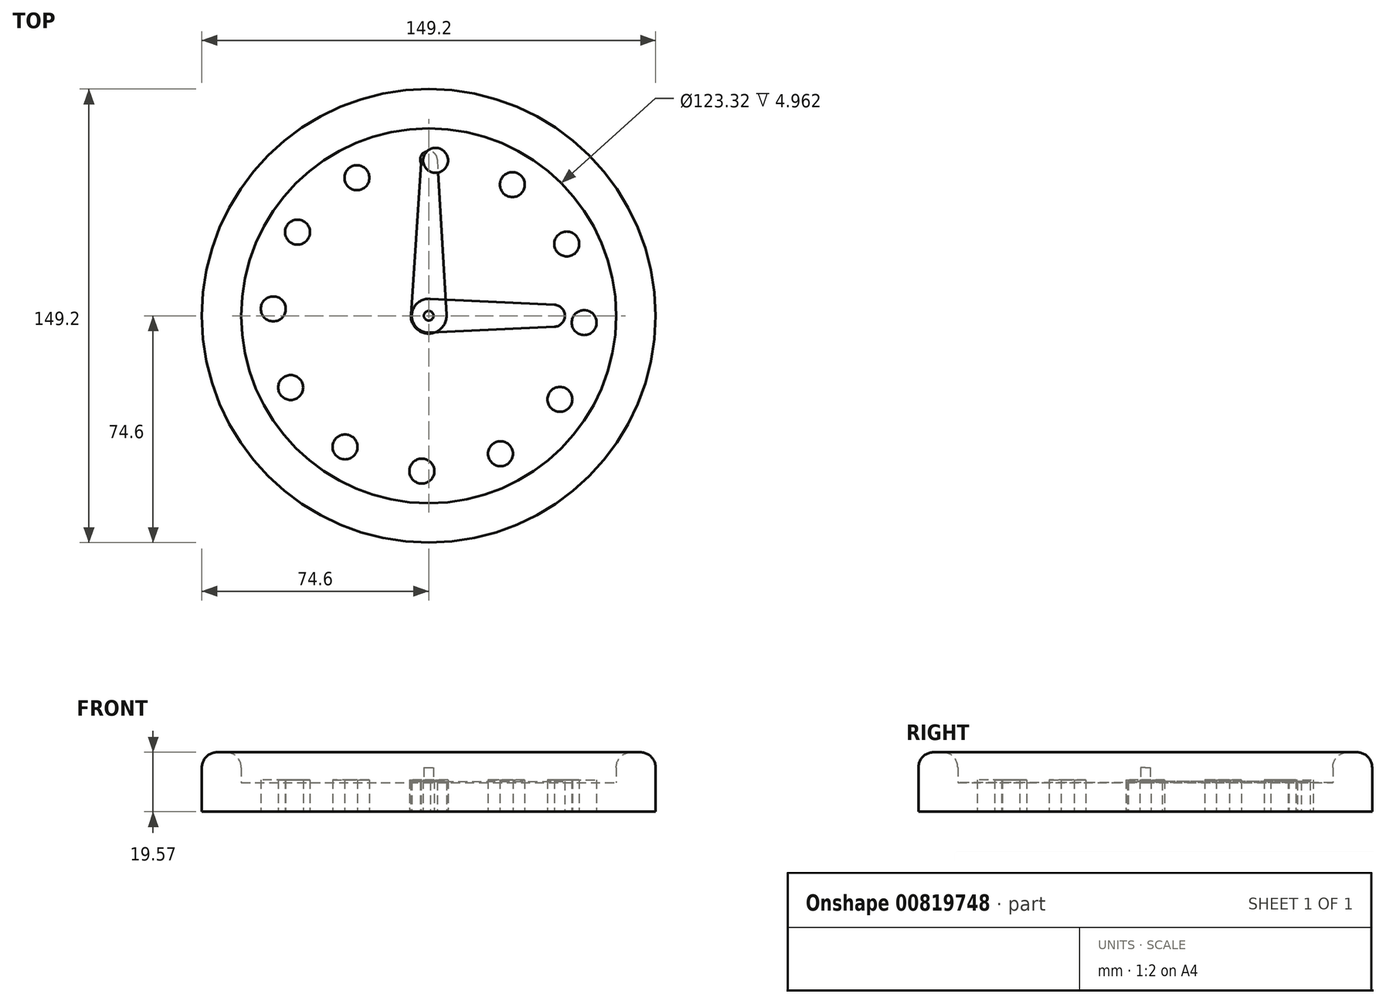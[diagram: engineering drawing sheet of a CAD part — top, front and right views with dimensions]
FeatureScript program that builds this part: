
annotation { "Feature Type Name" : "Feature", "Feature Type Description" : "" }
export const myFeature = defineFeature(function(context is Context, id is Id, definition is map)
    precondition{}
    {
        {
            var Q0;
            Q0=qCreatedBy(makeId("Front.planeOp"),FACE);
            var sketch = newSketch(context, id + "F0", { "sketchPlane" : qUnion([Q0])});
            skLineSegment(sketch, "E0", {"start": v(0, 0) * mm, "end": v(0, 64.16) * mm, "construction": true});
            skLineSegment(sketch, "E1.bottom", {"start": v(0, 0) * mm, "end": v(-74.6, 0) * mm});
            skLineSegment(sketch, "E1.top", {"start": v(0, 9.6) * mm, "end": v(-61.66, 9.6) * mm});
            skLineSegment(sketch, "E1.left", {"start": v(0, 0) * mm, "end": v(0, 9.6) * mm});
            skLineSegment(sketch, "E1.right", {"start": v(-74.6, 0) * mm, "end": v(-74.6, 9.6) * mm});
            skLineSegment(sketch, "E2.top", {"start": v(-69.6, 19.57) * mm, "end": v(-66.66, 19.57) * mm});
            skLineSegment(sketch, "E2.left", {"start": v(-74.6, 9.6) * mm, "end": v(-74.6, 14.57) * mm});
            skLineSegment(sketch, "E2.right", {"start": v(-61.66, 9.6) * mm, "end": v(-61.66, 14.57) * mm});
            skPoint(sketch, "E3.visualSharp", {"position": v(-61.66, 19.57) * mm});
            skArc(sketch, "E3.filletArc", {"start": v(-61.66, 14.57) * mm, "mid": v(-63.13, 18.1) * mm, "end": v(-66.66, 19.57) * mm});
            skPoint(sketch, "E4.visualSharp", {"position": v(-74.6, 19.57) * mm});
            skArc(sketch, "E4.filletArc", {"start": v(-69.6, 19.57) * mm, "mid": v(-73.13, 18.1) * mm, "end": v(-74.6, 14.57) * mm});
            skSolve(sketch);
        }
        {
            var Q0;
            Q0=makeQuery(id+"F0.imprint","IMPRINT",FACE,{"disambiguationData":[TD([[makeQuery(id+"F0.imprint","IMPRINT",EDGE,{"derivedFrom":sQuery(id+"F0.wireOp",EDGE,"E1.bottom")}),-1.0]])]});
            var Q1;
            Q1=sQuery(id+"F0.wireOp",EDGE,"E0");
            revolve(context, id + "F1", {"surfaceOperationType" : NewSurfaceOperationType.NEW, "entities" : qUnion([Q0]), "axis" : qUnion([Q1]), "revolveType" : RevolveType.FULL});
        }
        {
            var Q0;
            Q0=qCreatedBy(makeId("Top.planeOp"),FACE);
            var sketch = newSketch(context, id + "F2", { "sketchPlane" : qUnion([Q0])});
            skCircle(sketch, "E5", {"center": v(0, 53.25) * mm, "radius": 4.1 * mm});
            skCircle(sketch, "E6", {"center": v(0, -53.26) * mm, "radius": 4.1 * mm});
            skCircle(sketch, "E7", {"center": v(53.49, 0) * mm, "radius": 4.1 * mm});
            skCircle(sketch, "E8", {"center": v(-51.12, 2.25) * mm, "radius": 4.1 * mm});
            skSolve(sketch);
        }
        {
            var Q0;
            Q0=makeQuery(id+"F2.imprint","IMPRINT",FACE,{"disambiguationData":[TD([[makeQuery(id+"F2.imprint","IMPRINT",EDGE,{"derivedFrom":sQuery(id+"F2.wireOp",EDGE,"E8")}),1.0]])]});
            extrude(context, id + "F3", {"entities" : qUnion([Q0]), "depth" : 10.5 * mm, "offsetDistance" : 25 * mm});
        }
        {
            var Q0;
            Q0=qCreatedBy(makeId("Right.planeOp"),FACE);
            var sketch = newSketch(context, id + "F4", { "sketchPlane" : qUnion([Q0])});
            skLineSegment(sketch, "E9", {"start": v(0, 0) * mm, "end": v(0, 46.27) * mm, "construction": true});
            skSolve(sketch);
        }
        {
            var Q0;
            Q0=makeQuery(id+"F3.opExtrude","SWEPT_BODY",BODY,{"disambiguationData":[OSD([sQuery(id+"F2.wireOp",EDGE,"E8")])]});
            var Q1;
            Q1=sQuery(id+"F4.wireOp",EDGE,"E9");
            circularPattern(context, id + "F5", {"entities" : qUnion([Q0]), "axis" : qUnion([Q1]), "angle" : 360 * degree, "instanceCount" : 12, "equalSpace" : true});
        }
        {
            var Q0;
            Q0=qCreatedBy(makeId("Top.planeOp"),FACE);
            var sketch = newSketch(context, id + "F6", { "sketchPlane" : qUnion([Q0])});
            skCircle(sketch, "E10", {"center": v(0, 0) * mm, "radius": 1.58 * mm});
            skSolve(sketch);
        }
        {
            var Q0;
            Q0 = qSketchRegion(id + "F6", true);
            extrude(context, id + "F7", {"entities" : qUnion([Q0]), "operationType" : NewBodyOperationType.ADD, "depth" : 14.5 * mm, "offsetDistance" : 25 * mm});
        }
        {
            var Q0;
            Q0=qCreatedBy(makeId("Top.planeOp"),FACE);
            var sketch = newSketch(context, id + "F8", { "sketchPlane" : qUnion([Q0])});
            skArc(sketch, "E11", {"start": v(-5.85, 0.4) * mm, "mid": v(-0.02, -5.87) * mm, "end": v(5.86, 0.35) * mm});
            skArc(sketch, "E12", {"start": v(2.81, 51.35) * mm, "mid": v(-0.67, 54.09) * mm, "end": v(-2.5, 50.05) * mm});
            skLineSegment(sketch, "E13", {"start": v(-2.5, 50.05) * mm, "end": v(-5.88, 0) * mm});
            skLineSegment(sketch, "E14", {"start": v(2.81, 51.35) * mm, "end": v(5.88, 0) * mm});
            skSolve(sketch);
        }
        {
            var Q0;
            Q0 = qSketchRegion(id + "F8", true);
            extrude(context, id + "F9", {"entities" : qUnion([Q0]), "depth" : 10 * mm, "offsetDistance" : 25 * mm});
        }
        {
            var Q0;
            Q0=qCreatedBy(makeId("Top.planeOp"),FACE);
            var sketch = newSketch(context, id + "F10", { "sketchPlane" : qUnion([Q0])});
            skArc(sketch, "E15", {"start": v(0.52, 5.54) * mm, "mid": v(-5.57, 0) * mm, "end": v(0.52, -5.54) * mm});
            skArc(sketch, "E16", {"start": v(41.3, -3.63) * mm, "mid": v(44.77, 0) * mm, "end": v(41.3, 3.63) * mm});
            skLineSegment(sketch, "E17", {"start": v(0, 5.57) * mm, "end": v(41.3, 3.63) * mm});
            skLineSegment(sketch, "E18", {"start": v(0, -5.57) * mm, "end": v(41.3, -3.63) * mm});
            skSolve(sketch);
        }
        {
            var Q0;
            Q0 = qSketchRegion(id + "F10", true);
            extrude(context, id + "F11", {"entities" : qUnion([Q0]), "depth" : 10 * mm, "offsetDistance" : 25 * mm});
        }
    });
